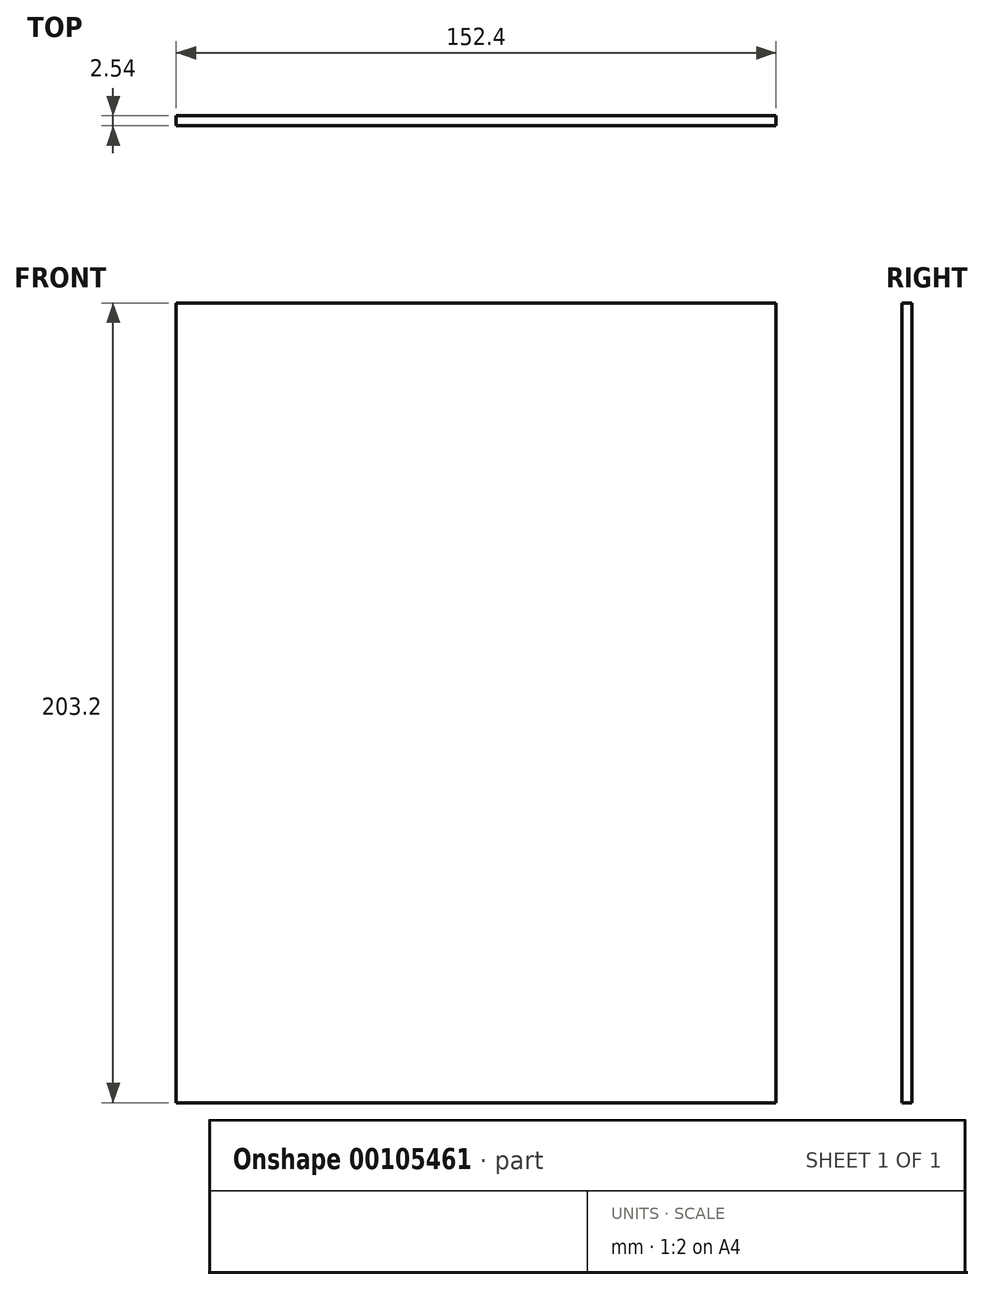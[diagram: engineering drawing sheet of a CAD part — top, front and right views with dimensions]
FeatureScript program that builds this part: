
annotation { "Feature Type Name" : "Feature", "Feature Type Description" : "" }
export const myFeature = defineFeature(function(context is Context, id is Id, definition is map)
    precondition{}
    {
        {
            var Q0;
            Q0=qCreatedBy(makeId("Front.planeOp"),FACE);
            var sketch = newSketch(context, id + "F0", { "sketchPlane" : qUnion([Q0])});
            skLineSegment(sketch, "E0.bottom", {"start": v(-76.2, 101.6) * mm, "end": v(76.2, 101.6) * mm});
            skLineSegment(sketch, "E0.top", {"start": v(-76.2, -101.6) * mm, "end": v(76.2, -101.6) * mm});
            skLineSegment(sketch, "E0.left", {"start": v(-76.2, 101.6) * mm, "end": v(-76.2, -101.6) * mm});
            skLineSegment(sketch, "E0.right", {"start": v(76.2, 101.6) * mm, "end": v(76.2, -101.6) * mm});
            skPoint(sketch, "E0.middle", {"position": v(0, 0) * mm});
            skSolve(sketch);
        }
        {
            var Q0;
            Q0=makeQuery(id+"F0.imprint","IMPRINT",FACE,{"disambiguationData":[TD([[makeQuery(id+"F0.imprint","IMPRINT",EDGE,{"derivedFrom":sQuery(id+"F0.wireOp",EDGE,"E0.bottom")}),-1.0]])]});
            extrude(context, id + "F1", {"entities" : qUnion([Q0]), "depth" : 2.54 * mm});
        }
    });
